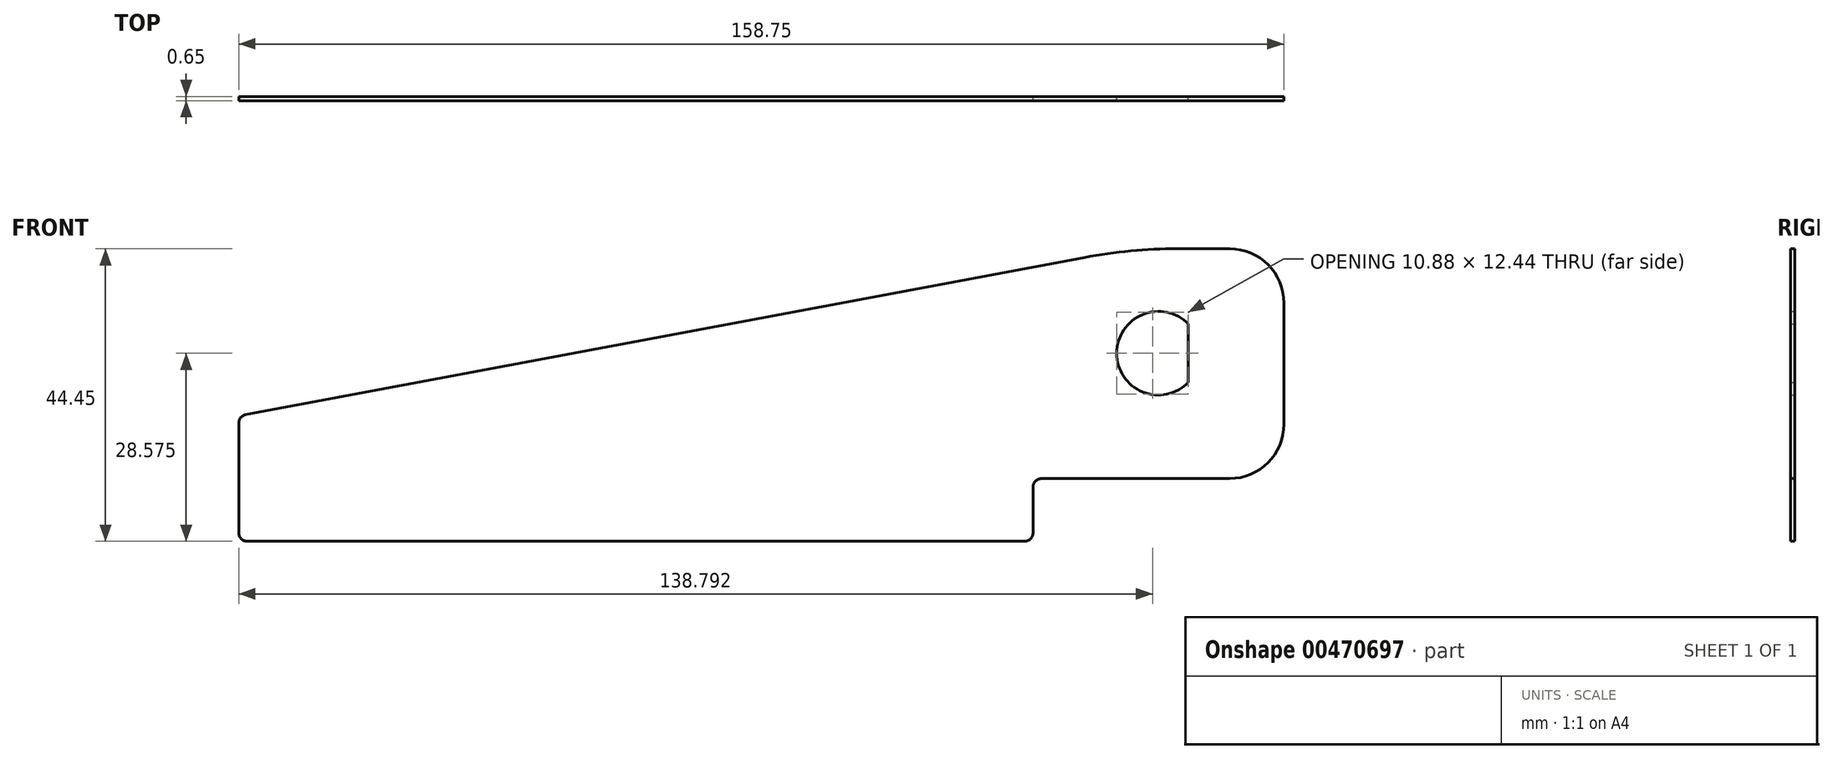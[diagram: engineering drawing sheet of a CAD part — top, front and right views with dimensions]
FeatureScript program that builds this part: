
annotation { "Feature Type Name" : "Feature", "Feature Type Description" : "" }
export const myFeature = defineFeature(function(context is Context, id is Id, definition is map)
    precondition{}
    {
        {
            var Q0;
            Q0=qCreatedBy(makeId("Front.planeOp"),FACE);
            var sketch = newSketch(context, id + "F0", { "sketchPlane" : qUnion([Q0])});
            skLineSegment(sketch, "E0", {"start": v(1.27, 0) * mm, "end": v(119.38, 0) * mm});
            skLineSegment(sketch, "E1", {"start": v(120.65, 1.27) * mm, "end": v(120.65, 8.26) * mm});
            skLineSegment(sketch, "E2", {"start": v(121.92, 9.53) * mm, "end": v(150.5, 9.53) * mm});
            skLineSegment(sketch, "E3", {"start": v(158.75, 17.78) * mm, "end": v(158.75, 36.2) * mm});
            skLineSegment(sketch, "E4", {"start": v(128.5, 43.14) * mm, "end": v(1.04, 19.24) * mm});
            skLineSegment(sketch, "E5", {"start": v(0, 18) * mm, "end": v(0, 1.27) * mm});
            skLineSegment(sketch, "E6", {"start": v(101.6, 38.1) * mm, "end": v(101.6, 0) * mm, "construction": true});
            skPoint(sketch, "E7", {"position": v(139.7, 28.58) * mm});
            skArc(sketch, "E8", {"start": v(144.23, 33.02) * mm, "mid": v(133.35, 28.58) * mm, "end": v(144.23, 24.13) * mm});
            skPoint(sketch, "E9.visualSharp", {"position": v(0, 19.05) * mm});
            skArc(sketch, "E9.filletArc", {"start": v(1.04, 19.24) * mm, "mid": v(0.3, 18.8) * mm, "end": v(0, 18) * mm});
            skPoint(sketch, "E10.visualSharp", {"position": v(0, 0) * mm});
            skArc(sketch, "E10.filletArc", {"start": v(0, 1.27) * mm, "mid": v(0.37, 0.37) * mm, "end": v(1.27, 0) * mm});
            skLineSegment(sketch, "E11", {"start": v(142.55, 44.45) * mm, "end": v(150.5, 44.45) * mm});
            skPoint(sketch, "E12.visualSharp", {"position": v(158.75, 44.45) * mm});
            skArc(sketch, "E12.filletArc", {"start": v(158.75, 36.2) * mm, "mid": v(156.33, 42.03) * mm, "end": v(150.5, 44.45) * mm});
            skPoint(sketch, "E13.visualSharp", {"position": v(158.75, 9.53) * mm});
            skArc(sketch, "E13.filletArc", {"start": v(150.5, 9.53) * mm, "mid": v(156.33, 11.94) * mm, "end": v(158.75, 17.78) * mm});
            skPoint(sketch, "E14.visualSharp", {"position": v(120.65, 0) * mm});
            skArc(sketch, "E14.filletArc", {"start": v(119.38, 0) * mm, "mid": v(120.28, 0.37) * mm, "end": v(120.65, 1.27) * mm});
            skPoint(sketch, "E15.visualSharp", {"position": v(120.65, 9.53) * mm});
            skArc(sketch, "E15.filletArc", {"start": v(121.92, 9.53) * mm, "mid": v(121.02, 9.15) * mm, "end": v(120.65, 8.26) * mm});
            skPoint(sketch, "E16.visualSharp", {"position": v(135.47, 44.45) * mm});
            skArc(sketch, "E16.filletArc", {"start": v(142.55, 44.45) * mm, "mid": v(135.5, 44.12) * mm, "end": v(128.5, 43.14) * mm});
            skLineSegment(sketch, "E17", {"start": v(144.23, 33.02) * mm, "end": v(144.23, 24.13) * mm});
            skSolve(sketch);
        }
        {
            var Q0;
            Q0 = qSketchRegion(id + "F0", true);
            extrude(context, id + "F1", {"entities" : qUnion([Q0]), "depth" : 0.65 * mm});
        }
    });
